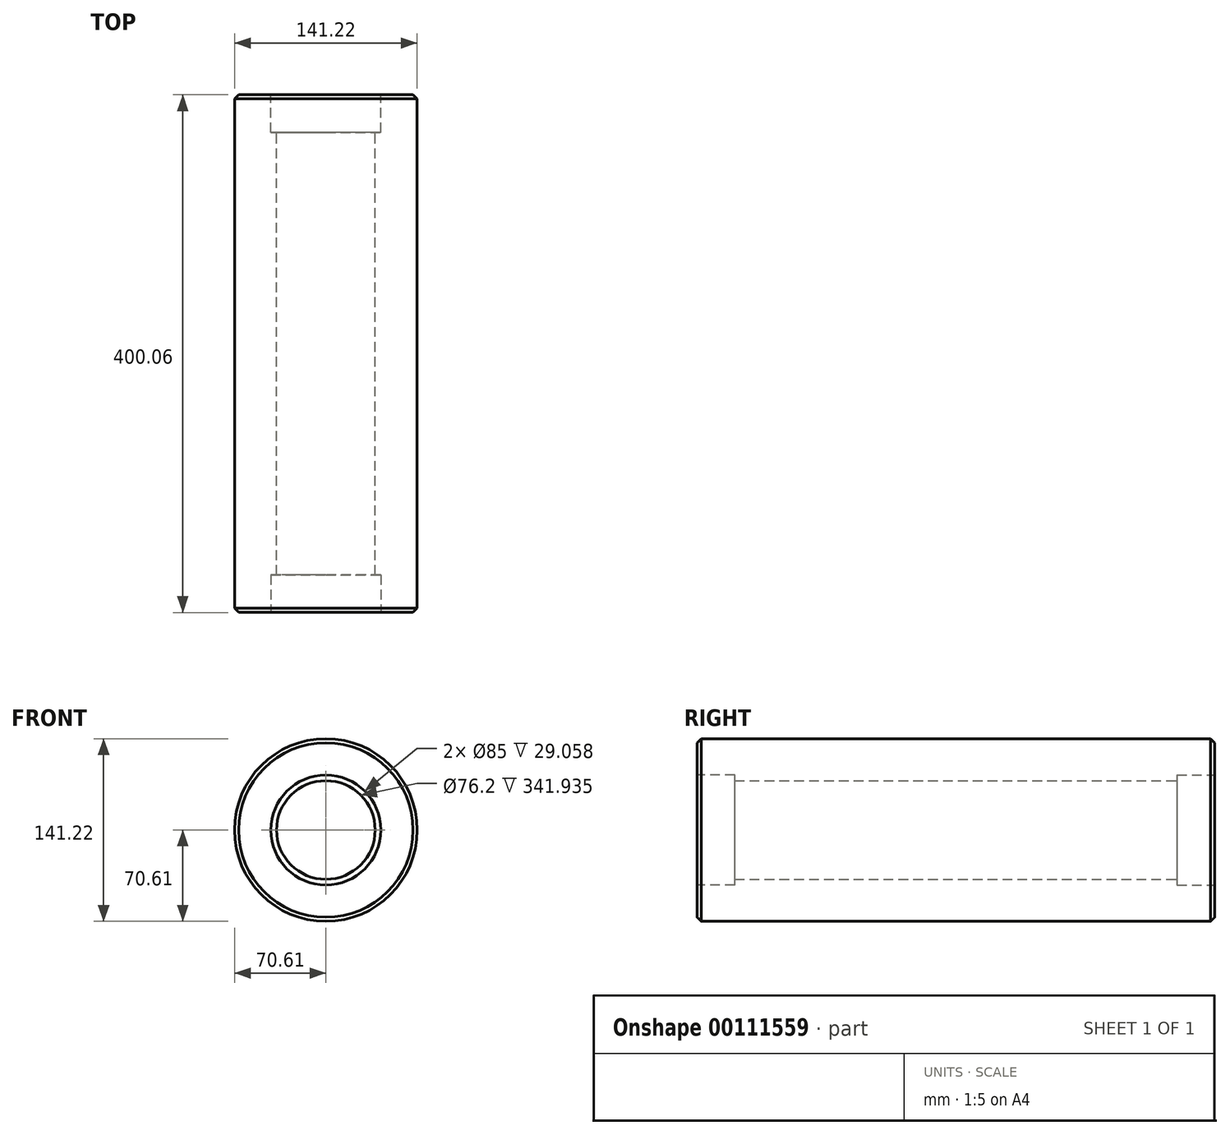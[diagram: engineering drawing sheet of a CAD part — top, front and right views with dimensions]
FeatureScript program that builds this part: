
annotation { "Feature Type Name" : "Feature", "Feature Type Description" : "" }
export const myFeature = defineFeature(function(context is Context, id is Id, definition is map)
    precondition{}
    {
        {
            var Q0;
            Q0=qCreatedBy(makeId("Front.planeOp"),FACE);
            var sketch = newSketch(context, id + "F0", { "sketchPlane" : qUnion([Q0])});
            skCircle(sketch, "E0", {"center": v(0, 0) * mm, "radius": 70.61 * mm});
            skSolve(sketch);
        }
        {
            var Q0;
            Q0 = qSketchRegion(id + "F0", true);
            extrude(context, id + "F1", {"entities" : qUnion([Q0]), "endBound" : BoundingType.SYMMETRIC, "depth" : 400.05 * mm});
        }
        {
            var Q0;
            Q0=makeQuery(id+"F1.opExtrude","CAP_FACE",FACE,{"disambiguationData":[OSD([sQuery(id+"F0.wireOp",EDGE,"E0")])],"isStart":false});
            var Q1;
            Q1=makeQuery(id+"F1.opExtrude","CAP_FACE",FACE,{"disambiguationData":[OSD([sQuery(id+"F0.wireOp",EDGE,"E0")])],"isStart":true});
            chamfer(context, id + "F2", {"entities" : qUnion([Q0, Q1]), "width" : 3.17 * mm, "tangentPropagation" : true});
        }
        {
            var Q0;
            Q0=makeQuery(id+"F1.opExtrude","CAP_FACE",FACE,{"disambiguationData":[OSD([sQuery(id+"F0.wireOp",EDGE,"E0")])],"isStart":true});
            var sketch = newSketch(context, id + "F3", { "sketchPlane" : qUnion([Q0])});
            skCircle(sketch, "E1.0.0", {"center": v(0, 0) * mm, "radius": 67.44 * mm, "construction": true});
            skSolve(sketch);
        }
        {
            var Q0;
            Q0=sQuery(id+"F3.wireOp",VERTEX,"E1.0.0.center");
            var Q1;
            Q1=makeQuery(id+"F1.opExtrude","SWEPT_BODY",BODY,{"disambiguationData":[OSD([sQuery(id+"F0.wireOp",EDGE,"E0")])]});
            hole(context, id + "F4", {"style" : HoleStyle.C_BORE, "endStyle" : HoleEndStyle.THROUGH, "holeDiameter" : 76.2 * mm, "cBoreDiameter" : 85 * mm, "cBoreDepth" : 29.06 * mm, "locations" : qUnion([Q0]), "scope" : qUnion([Q1]), "isTappedThrough" : true});
        }
        {
            var Q0;
            Q0=makeQuery(id+"F1.opExtrude","CAP_FACE",FACE,{"disambiguationData":[OSD([sQuery(id+"F0.wireOp",EDGE,"E0")])],"isStart":false});
            var sketch = newSketch(context, id + "F5", { "sketchPlane" : qUnion([Q0])});
            skCircle(sketch, "E2.0", {"center": v(0, 0) * mm, "radius": 42.5 * mm});
            skSolve(sketch);
        }
        {
            var Q0;
            Q0 = qSketchRegion(id + "F5", true);
            extrude(context, id + "F6", {"entities" : qUnion([Q0]), "operationType" : NewBodyOperationType.REMOVE, "oppositeDirection" : true, "depth" : 29.06 * mm});
        }
    });
